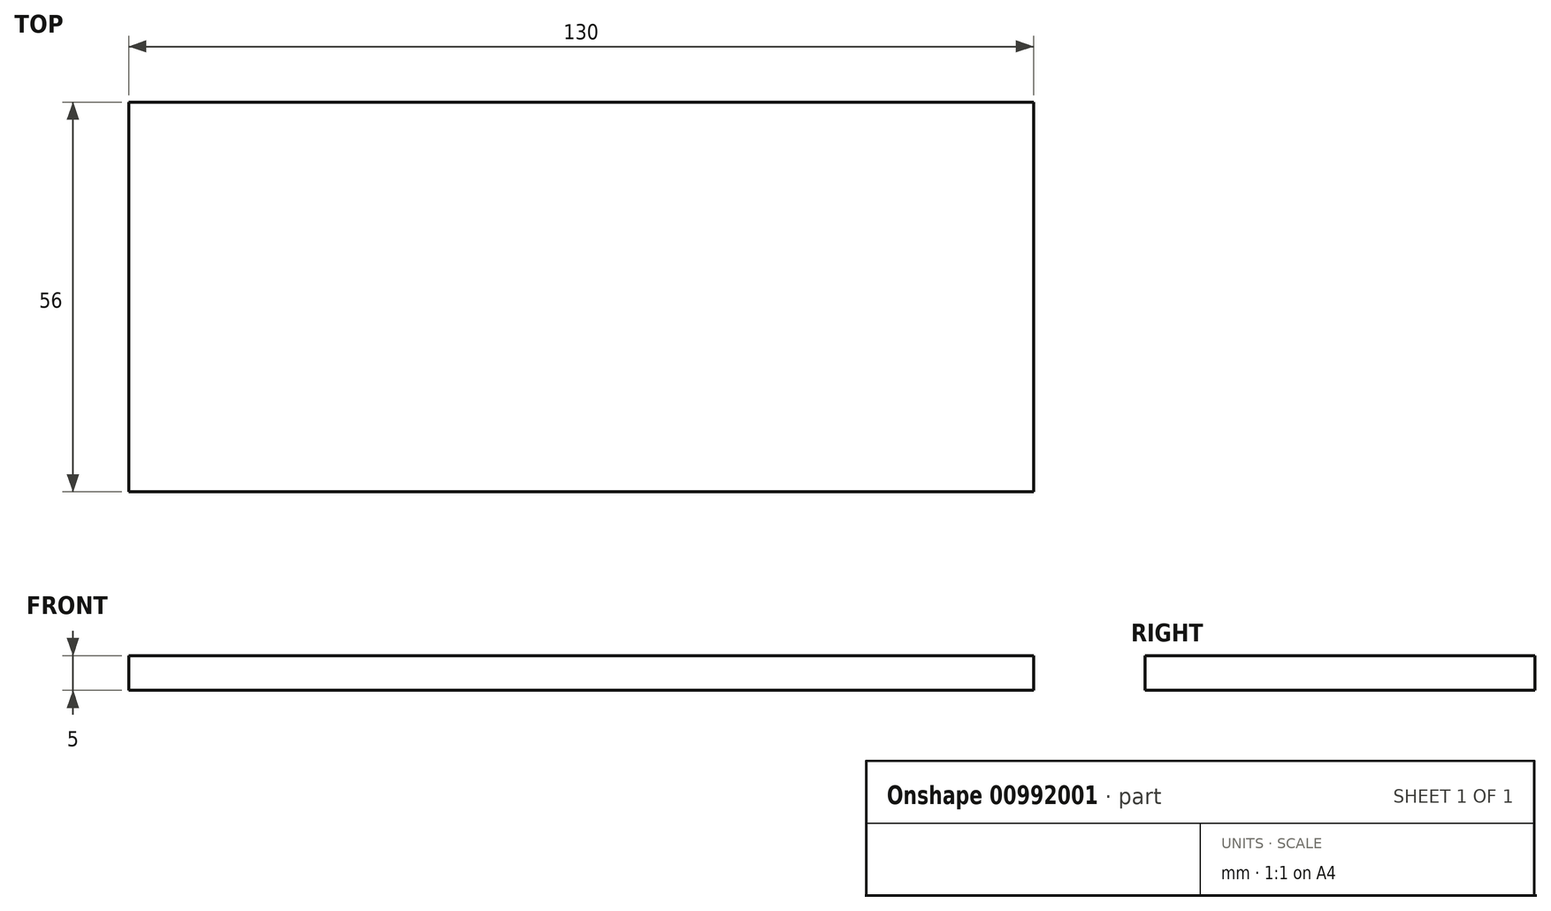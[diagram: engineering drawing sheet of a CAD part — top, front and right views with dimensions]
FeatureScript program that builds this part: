
annotation { "Feature Type Name" : "Feature", "Feature Type Description" : "" }
export const myFeature = defineFeature(function(context is Context, id is Id, definition is map)
    precondition{}
    {
        {
            var Q0;
            Q0=qCreatedBy(makeId("Top.planeOp"),FACE);
            var sketch = newSketch(context, id + "F0", { "sketchPlane" : qUnion([Q0])});
            skLineSegment(sketch, "E0.bottom", {"start": v(-65, 28) * mm, "end": v(65, 28) * mm});
            skLineSegment(sketch, "E0.top", {"start": v(-65, -28) * mm, "end": v(65, -28) * mm});
            skLineSegment(sketch, "E0.left", {"start": v(-65, 28) * mm, "end": v(-65, -28) * mm});
            skLineSegment(sketch, "E0.right", {"start": v(65, 28) * mm, "end": v(65, -28) * mm});
            skSolve(sketch);
        }
        {
            var Q0;
            Q0=makeQuery(id+"F0.imprint","IMPRINT",FACE,{"disambiguationData":[TD([[makeQuery(id+"F0.imprint","IMPRINT",EDGE,{"derivedFrom":sQuery(id+"F0.wireOp",EDGE,"E0.bottom")}),-1.0]])]});
            extrude(context, id + "F1", {"entities" : qUnion([Q0]), "depth" : 5 * mm, "offsetDistance" : 25 * mm});
        }
    });
